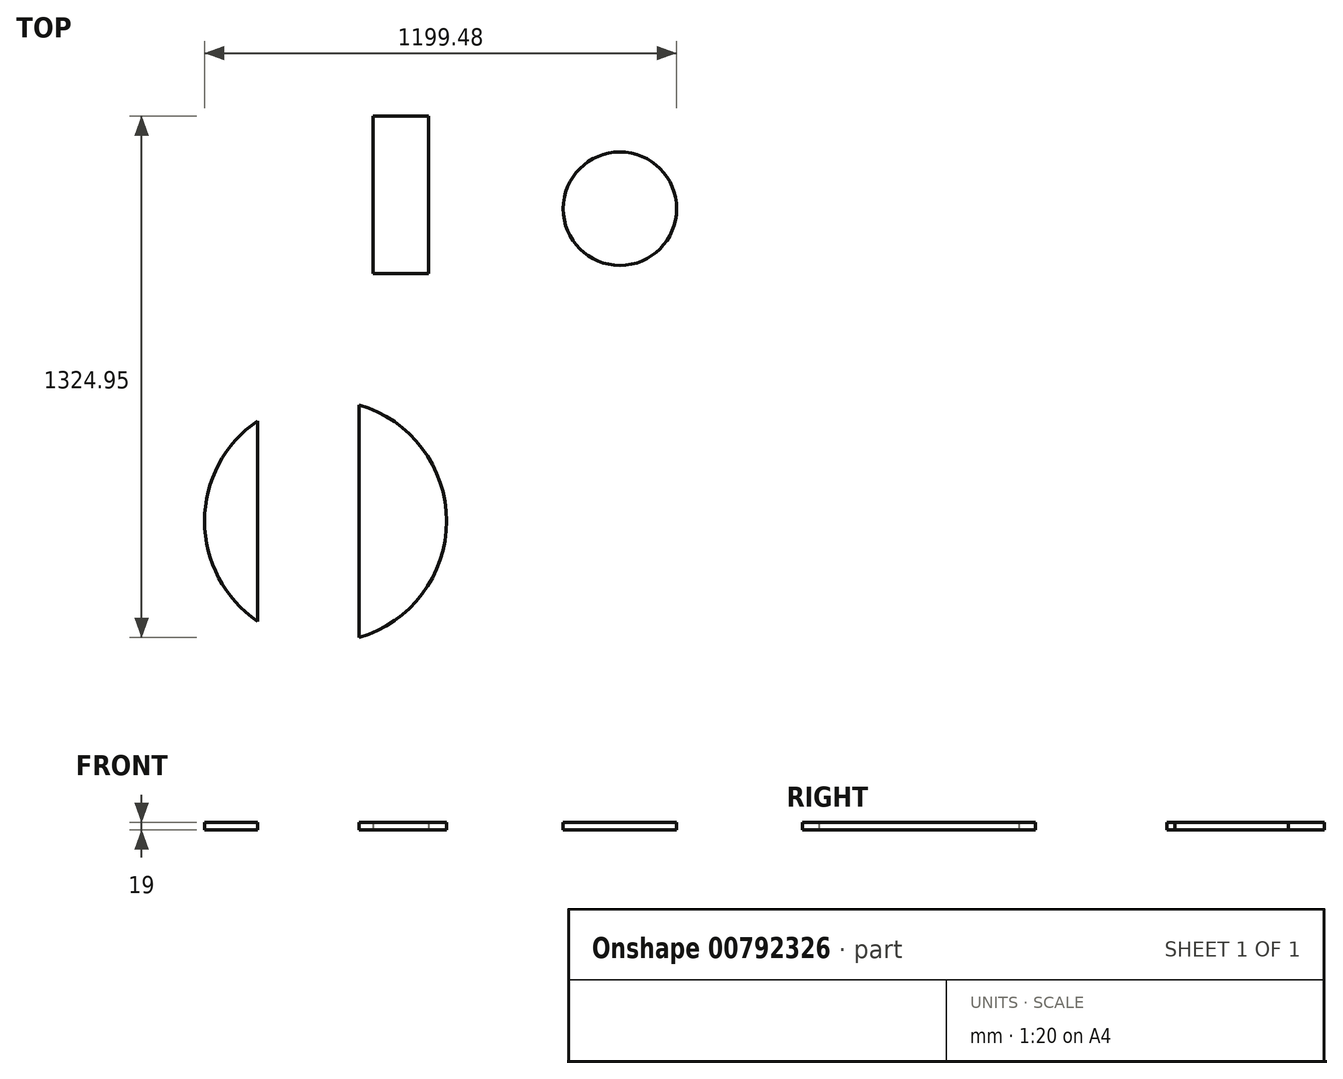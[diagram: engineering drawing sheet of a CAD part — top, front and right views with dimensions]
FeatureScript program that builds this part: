
annotation { "Feature Type Name" : "Feature", "Feature Type Description" : "" }
export const myFeature = defineFeature(function(context is Context, id is Id, definition is map)
    precondition{}
    {
        {
            var Q0;
            Q0=qCreatedBy(makeId("Top.planeOp"),FACE);
            var sketch = newSketch(context, id + "F0", { "sketchPlane" : qUnion([Q0])});
            skArc(sketch, "E0", {"start": v(-352.63, 173.04) * mm, "mid": v(-454.93, 53.24) * mm, "end": v(-386.5, -88.66) * mm});
            skArc(sketch, "E1", {"start": v(-386.5, -88.66) * mm, "mid": v(-320.23, -109.2) * mm, "end": v(-252.04, -96.39) * mm});
            skArc(sketch, "E2", {"start": v(-252.04, -96.39) * mm, "mid": v(-167.96, 27.88) * mm, "end": v(-239.86, 159.57) * mm});
            skArc(sketch, "E3", {"start": v(-239.86, 159.57) * mm, "mid": v(-294.86, 177.88) * mm, "end": v(-352.63, 173.04) * mm});
            skSolve(sketch);
        }
        {
            var Q0;
            Q0=makeQuery(id+"F0.imprint","IMPRINT",FACE,{"disambiguationData":[TD([[makeQuery(id+"F0.imprint","IMPRINT",EDGE,{"derivedFrom":sQuery(id+"F0.wireOp",EDGE,"E0")}),1.0]])]});
            var sketch = newSketch(context, id + "F1", { "sketchPlane" : qUnion([Q0])});
            skLineSegment(sketch, "E4", {"start": v(-351.48, 170.3) * mm, "end": v(-351.48, -103.06) * mm});
            skLineSegment(sketch, "E5", {"start": v(-242.7, 158.96) * mm, "end": v(-242.7, -90.38) * mm});
            skLineSegment(sketch, "E6", {"start": v(-975.12, -463.63) * mm, "end": v(-975.12, -1054.6) * mm});
            skLineSegment(sketch, "E7", {"start": v(-1232.76, -504.93) * mm, "end": v(-1232.76, -1013.3) * mm});
            skLineSegment(sketch, "E8", {"start": v(-975.12, -1054.6) * mm, "end": v(-975.12, -1054.6) * mm});
            skArc(sketch, "E9", {"start": v(-1232.76, -504.93) * mm, "mid": v(-1367.28, -759.11) * mm, "end": v(-1232.76, -1013.3) * mm});
            skArc(sketch, "E10", {"start": v(-975.12, -1054.6) * mm, "mid": v(-752.48, -759.11) * mm, "end": v(-975.12, -463.63) * mm});
            skSolve(sketch);
        }
        {
            var Q0;
            Q0=makeQuery(id+"F0.imprint","IMPRINT",FACE,{"disambiguationData":[TD([[makeQuery(id+"F0.imprint","IMPRINT",EDGE,{"derivedFrom":sQuery(id+"F0.wireOp",EDGE,"E0")}),1.0]])]});
            var sketch = newSketch(context, id + "F2", { "sketchPlane" : qUnion([Q0])});
            skSolve(sketch);
        }
        {
            var Q0;
            Q0=makeQuery(id+"F2.imprint","IMPRINT",FACE,{"disambiguationData":[TD([[makeQuery(id+"F2.imprint","IMPRINT",EDGE,{"derivedFrom":makeQuery(id+"F0.imprint","IMPRINT",EDGE,{"derivedFrom":sQuery(id+"F0.wireOp",EDGE,"E0")})}),1.0]])]});
            extrude(context, id + "F3", {"entities" : qUnion([Q0]), "depth" : 19 * mm, "offsetDistance" : 25 * mm});
        }
        {
            var Q0;
            Q0=makeQuery(id+"F1.imprint","IMPRINT",FACE,{"disambiguationData":[TD([[makeQuery(id+"F1.imprint","IMPRINT",EDGE,{"derivedFrom":sQuery(id+"F1.wireOp",EDGE,"E7")}),-1.0]])]});
            var Q1;
            Q1=makeQuery(id+"F1.imprint","IMPRINT",FACE,{"disambiguationData":[TD([[makeQuery(id+"F1.imprint","IMPRINT",EDGE,{"derivedFrom":sQuery(id+"F1.wireOp",EDGE,"E6")}),1.0]])]});
            extrude(context, id + "F4", {"entities" : qUnion([Q0, Q1]), "depth" : 19 * mm, "offsetDistance" : 25 * mm});
        }
        {
            var Q0;
            Q0=qCreatedBy(makeId("Top.planeOp"),FACE);
            var sketch = newSketch(context, id + "F5", { "sketchPlane" : qUnion([Q0])});
            skLineSegment(sketch, "E11.bottom", {"start": v(-938.6, 270.35) * mm, "end": v(-798.6, 270.35) * mm});
            skLineSegment(sketch, "E11.top", {"start": v(-938.6, -129.65) * mm, "end": v(-798.6, -129.65) * mm});
            skLineSegment(sketch, "E11.left", {"start": v(-938.6, 270.35) * mm, "end": v(-938.6, -129.65) * mm});
            skLineSegment(sketch, "E11.right", {"start": v(-798.6, 270.35) * mm, "end": v(-798.6, -129.65) * mm});
            skSolve(sketch);
        }
        {
            var Q0;
            Q0=makeQuery(id+"F5.imprint","IMPRINT",FACE,{"disambiguationData":[TD([[makeQuery(id+"F5.imprint","IMPRINT",EDGE,{"derivedFrom":sQuery(id+"F5.wireOp",EDGE,"E11.bottom")}),-1.0]])]});
            extrude(context, id + "F6", {"entities" : qUnion([Q0]), "depth" : 19 * mm, "offsetDistance" : 25 * mm});
        }
    });
